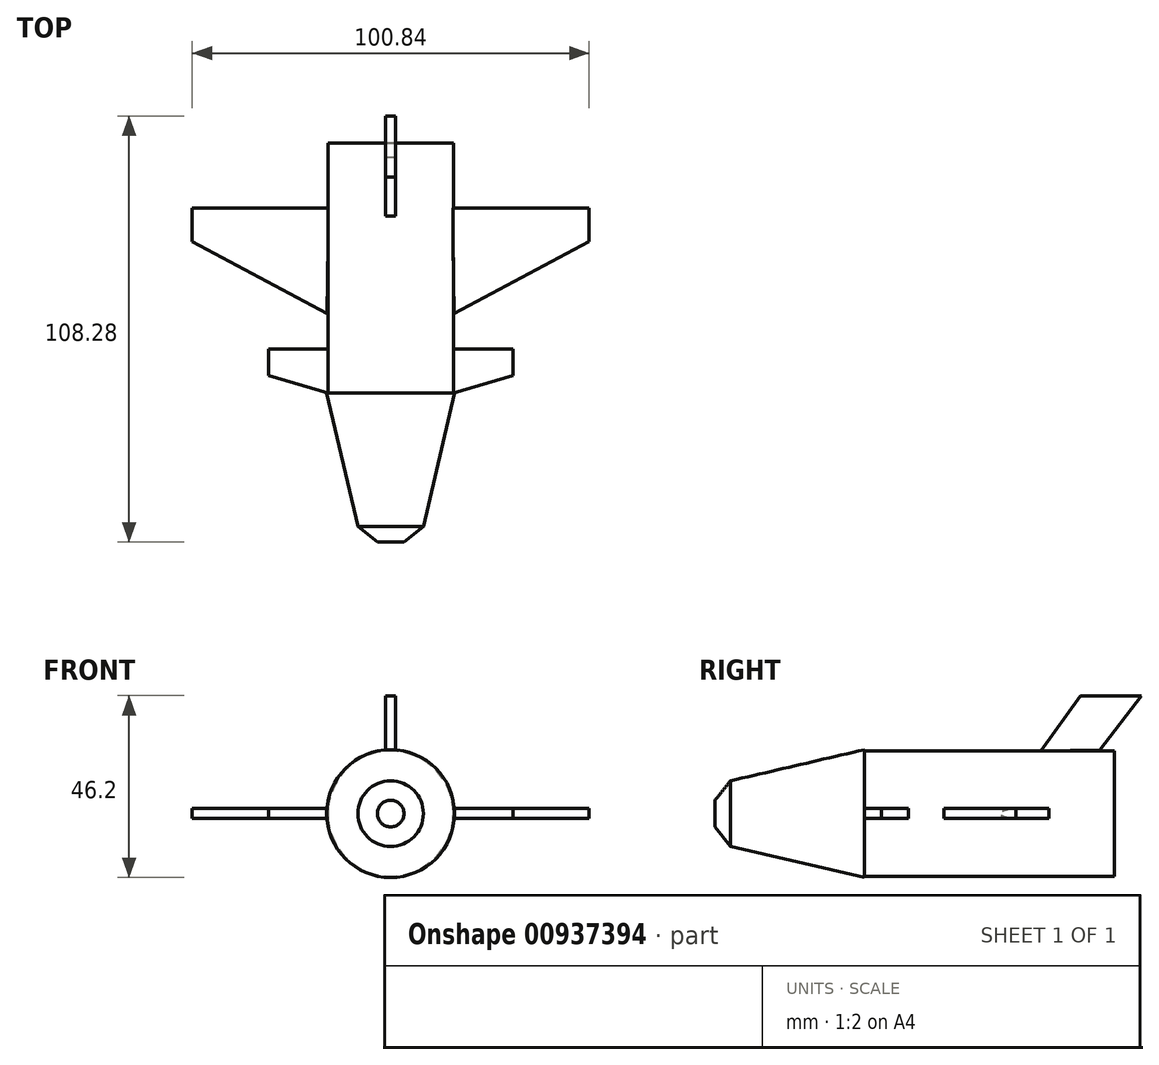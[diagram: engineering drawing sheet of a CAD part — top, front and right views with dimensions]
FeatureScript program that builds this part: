
annotation { "Feature Type Name" : "Feature", "Feature Type Description" : "" }
export const myFeature = defineFeature(function(context is Context, id is Id, definition is map)
    precondition{}
    {
        {
            var Q0;
            Q0=qCreatedBy(makeId("Front.planeOp"),FACE);
            var sketch = newSketch(context, id + "F0", { "sketchPlane" : qUnion([Q0])});
            skCircle(sketch, "E0", {"center": v(0, 0) * mm, "radius": 15.94 * mm});
            skSolve(sketch);
        }
        {
            var Q0;
            Q0 = qSketchRegion(id + "F0", true);
            extrude(context, id + "F1", {"entities" : qUnion([Q0]), "depth" : 0 * mm, "offsetDistance" : 25.4 * mm, "hasSecondDirection" : true, "secondDirectionOppositeDirection" : true, "secondDirectionDepth" : 63.5 * mm});
        }
        {
            var Q0;
            Q0=qCreatedBy(makeId("Top.planeOp"),FACE);
            var sketch = newSketch(context, id + "F2", { "sketchPlane" : qUnion([Q0])});
            skLineSegment(sketch, "E1", {"start": v(0, 0) * mm, "end": v(0, -37.95) * mm});
            skLineSegment(sketch, "E2", {"start": v(0, -37.95) * mm, "end": v(7.42, -37.95) * mm});
            skLineSegment(sketch, "E3", {"start": v(7.42, -37.95) * mm, "end": v(16.24, 0) * mm});
            skLineSegment(sketch, "E4", {"start": v(16.24, 0) * mm, "end": v(0, 0) * mm});
            skSolve(sketch);
        }
        {
            var Q0;
            Q0=makeQuery(id+"F2.imprint","IMPRINT",FACE,{"disambiguationData":[TD([[makeQuery(id+"F2.imprint","IMPRINT",EDGE,{"derivedFrom":sQuery(id+"F2.wireOp",EDGE,"E1")}),1.0]])]});
            var Q1;
            Q1=sQuery(id+"F2.wireOp",EDGE,"E1");
            revolve(context, id + "F3", {"operationType" : NewBodyOperationType.ADD, "surfaceOperationType" : NewSurfaceOperationType.NEW, "entities" : qUnion([Q0]), "axis" : qUnion([Q1]), "revolveType" : RevolveType.FULL});
        }
        {
            var Q0;
            Q0=qCreatedBy(makeId("Top.planeOp"),FACE);
            var sketch = newSketch(context, id + "F4", { "sketchPlane" : qUnion([Q0])});
            skLineSegment(sketch, "E5", {"start": v(16.13, 20.19) * mm, "end": v(50.42, 38.44) * mm});
            skLineSegment(sketch, "E6", {"start": v(50.42, 38.44) * mm, "end": v(50.42, 46.92) * mm});
            skLineSegment(sketch, "E7", {"start": v(50.42, 46.92) * mm, "end": v(15.76, 46.92) * mm});
            skLineSegment(sketch, "E8", {"start": v(15.76, 46.92) * mm, "end": v(16.13, 20.19) * mm});
            skLineSegment(sketch, "E9.MirrorCS", {"start": v(-16.13, 20.19) * mm, "end": v(-50.42, 38.44) * mm});
            skLineSegment(sketch, "E10.MirrorCS", {"start": v(-50.42, 38.44) * mm, "end": v(-50.42, 46.92) * mm});
            skLineSegment(sketch, "E11.MirrorCS", {"start": v(-50.42, 46.92) * mm, "end": v(-15.76, 46.92) * mm});
            skLineSegment(sketch, "E12.MirrorCS", {"start": v(-15.76, 46.92) * mm, "end": v(-16.13, 20.19) * mm});
            skSolve(sketch);
        }
        {
            var Q0;
            Q0 = qSketchRegion(id + "F4", true);
            extrude(context, id + "F5", {"entities" : qUnion([Q0]), "operationType" : NewBodyOperationType.ADD, "depth" : 1.27 * mm, "offsetDistance" : 25.4 * mm, "hasSecondDirection" : true, "secondDirectionOppositeDirection" : true, "secondDirectionDepth" : 1.27 * mm});
        }
        {
            var Q0;
            Q0=makeQuery(id+"F3.opRevolve","SWEPT_FACE",FACE,{"disambiguationData":[OSD([sQuery(id+"F2.wireOp",EDGE,"E2")])]});
            chamfer(context, id + "F6", {"entities" : qUnion([Q0]), "width" : 5.08 * mm, "tangentPropagation" : true});
        }
        {
            var Q0;
            Q0=qCreatedBy(makeId("Top.planeOp"),FACE);
            var sketch = newSketch(context, id + "F7", { "sketchPlane" : qUnion([Q0])});
            skLineSegment(sketch, "E13", {"start": v(15.95, 0) * mm, "end": v(31.06, 4.33) * mm});
            skLineSegment(sketch, "E14", {"start": v(31.06, 4.33) * mm, "end": v(31.06, 11.15) * mm});
            skLineSegment(sketch, "E15", {"start": v(15.95, 11.15) * mm, "end": v(31.06, 11.15) * mm});
            skLineSegment(sketch, "E16", {"start": v(15.95, 0) * mm, "end": v(15.95, 11.15) * mm});
            skLineSegment(sketch, "E17.MirrorCS", {"start": v(-15.95, 0) * mm, "end": v(-31.06, 4.33) * mm});
            skLineSegment(sketch, "E18.MirrorCS", {"start": v(-31.06, 4.33) * mm, "end": v(-31.06, 11.15) * mm});
            skLineSegment(sketch, "E19.MirrorCS", {"start": v(-15.95, 11.15) * mm, "end": v(-31.06, 11.15) * mm});
            skLineSegment(sketch, "E20.MirrorCS", {"start": v(-15.95, 0) * mm, "end": v(-15.95, 11.15) * mm});
            skSolve(sketch);
        }
        {
            var Q0;
            Q0 = qSketchRegion(id + "F7", true);
            extrude(context, id + "F8", {"entities" : qUnion([Q0]), "depth" : 1.27 * mm, "offsetDistance" : 25.4 * mm, "hasSecondDirection" : true, "secondDirectionOppositeDirection" : true, "secondDirectionDepth" : 1.27 * mm});
        }
        {
            var Q0;
            Q0=qCreatedBy(makeId("Right.planeOp"),FACE);
            var sketch = newSketch(context, id + "F9", { "sketchPlane" : qUnion([Q0])});
            skLineSegment(sketch, "E21", {"start": v(59.82, 16.13) * mm, "end": v(70.33, 29.96) * mm});
            skLineSegment(sketch, "E22", {"start": v(54.85, 29.96) * mm, "end": v(44.9, 15.95) * mm});
            skLineSegment(sketch, "E23", {"start": v(54.85, 29.96) * mm, "end": v(70.33, 29.96) * mm});
            skLineSegment(sketch, "E24", {"start": v(44.9, 15.95) * mm, "end": v(59.82, 16.13) * mm});
            skSolve(sketch);
        }
        {
            var Q0;
            Q0 = qSketchRegion(id + "F9", true);
            extrude(context, id + "F10", {"entities" : qUnion([Q0]), "depth" : 1.27 * mm, "offsetDistance" : 25.4 * mm, "hasSecondDirection" : true, "secondDirectionOppositeDirection" : true, "secondDirectionDepth" : 1.27 * mm});
        }
    });
